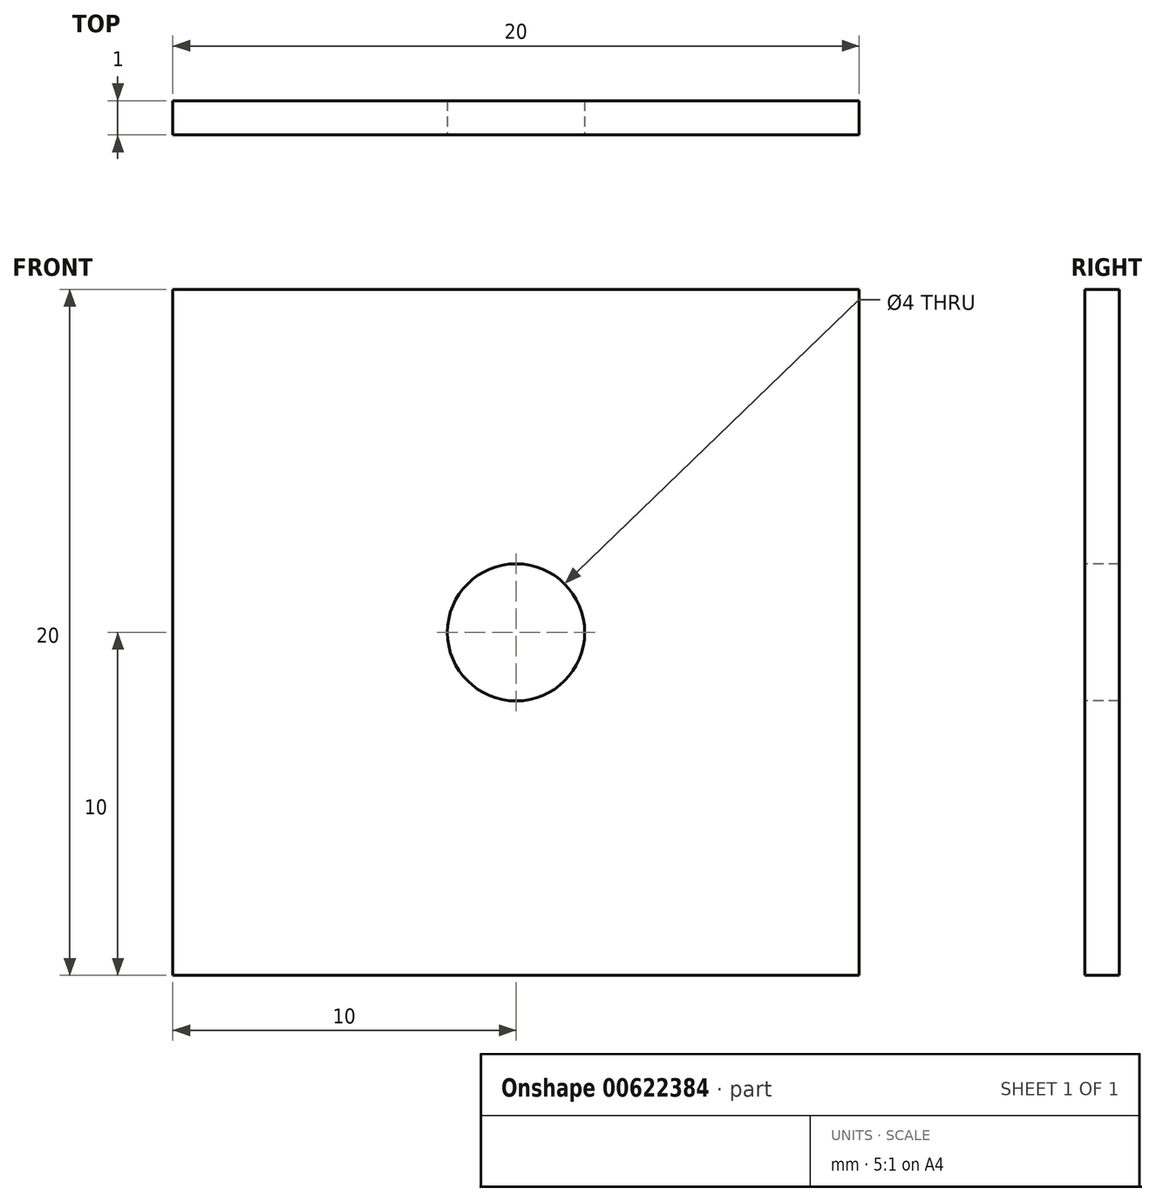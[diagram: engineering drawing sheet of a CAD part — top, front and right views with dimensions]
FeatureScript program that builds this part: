
annotation { "Feature Type Name" : "Feature", "Feature Type Description" : "" }
export const myFeature = defineFeature(function(context is Context, id is Id, definition is map)
    precondition{}
    {
        {
            var Q0;
            Q0=qCreatedBy(makeId("Front.planeOp"),FACE);
            var sketch = newSketch(context, id + "F0", { "sketchPlane" : qUnion([Q0])});
            skLineSegment(sketch, "E0.bottom", {"start": v(10, -10) * mm, "end": v(-10, -10) * mm});
            skLineSegment(sketch, "E0.top", {"start": v(10, 10) * mm, "end": v(-10, 10) * mm});
            skLineSegment(sketch, "E0.left", {"start": v(10, -10) * mm, "end": v(10, 10) * mm});
            skLineSegment(sketch, "E0.right", {"start": v(-10, -10) * mm, "end": v(-10, 10) * mm});
            skPoint(sketch, "E0.middle", {"position": v(0, 0) * mm});
            skSolve(sketch);
        }
        {
            var Q0;
            Q0=qSketchRegion(id+"F0",true);
            extrude(context, id + "F1", {"entities" : qUnion([Q0]), "depth" : 1 * mm, "offsetDistance" : 25.4 * mm});
        }
        {
            var Q0;
            Q0=makeQuery(id+"F1.opExtrude","CAP_FACE",FACE,{"disambiguationData":[OSD([sQuery(id+"F0.wireOp",EDGE,"E0.bottom"),sQuery(id+"F0.wireOp",EDGE,"E0.top"),sQuery(id+"F0.wireOp",EDGE,"E0.left"),sQuery(id+"F0.wireOp",EDGE,"E0.right")])],"isStart":false});
            var sketch = newSketch(context, id + "F2", { "sketchPlane" : qUnion([Q0])});
            skCircle(sketch, "E1", {"center": v(0, 0) * mm, "radius": 2 * mm});
            skSolve(sketch);
        }
        {
            var Q0;
            Q0=sQuery(id+"F2.wireOp",VERTEX,"E1.center");
            var Q1;
            Q1=makeQuery(id+"F1.opExtrude","SWEPT_BODY",BODY,{"disambiguationData":[OSD([sQuery(id+"F0.wireOp",EDGE,"E0.bottom"),sQuery(id+"F0.wireOp",EDGE,"E0.top"),sQuery(id+"F0.wireOp",EDGE,"E0.left"),sQuery(id+"F0.wireOp",EDGE,"E0.right")])]});
            hole(context, id + "F3", {"style" : HoleStyle.SIMPLE, "endStyle" : HoleEndStyle.THROUGH, "holeDiameter" : 4 * mm, "majorDiameter" : 6.35 * mm, "isTappedThrough" : true, "tappedDepth" : 12.7 * mm, "tapClearance" : 3, "locations" : qUnion([Q0]), "scope" : qUnion([Q1])});
        }
    });
